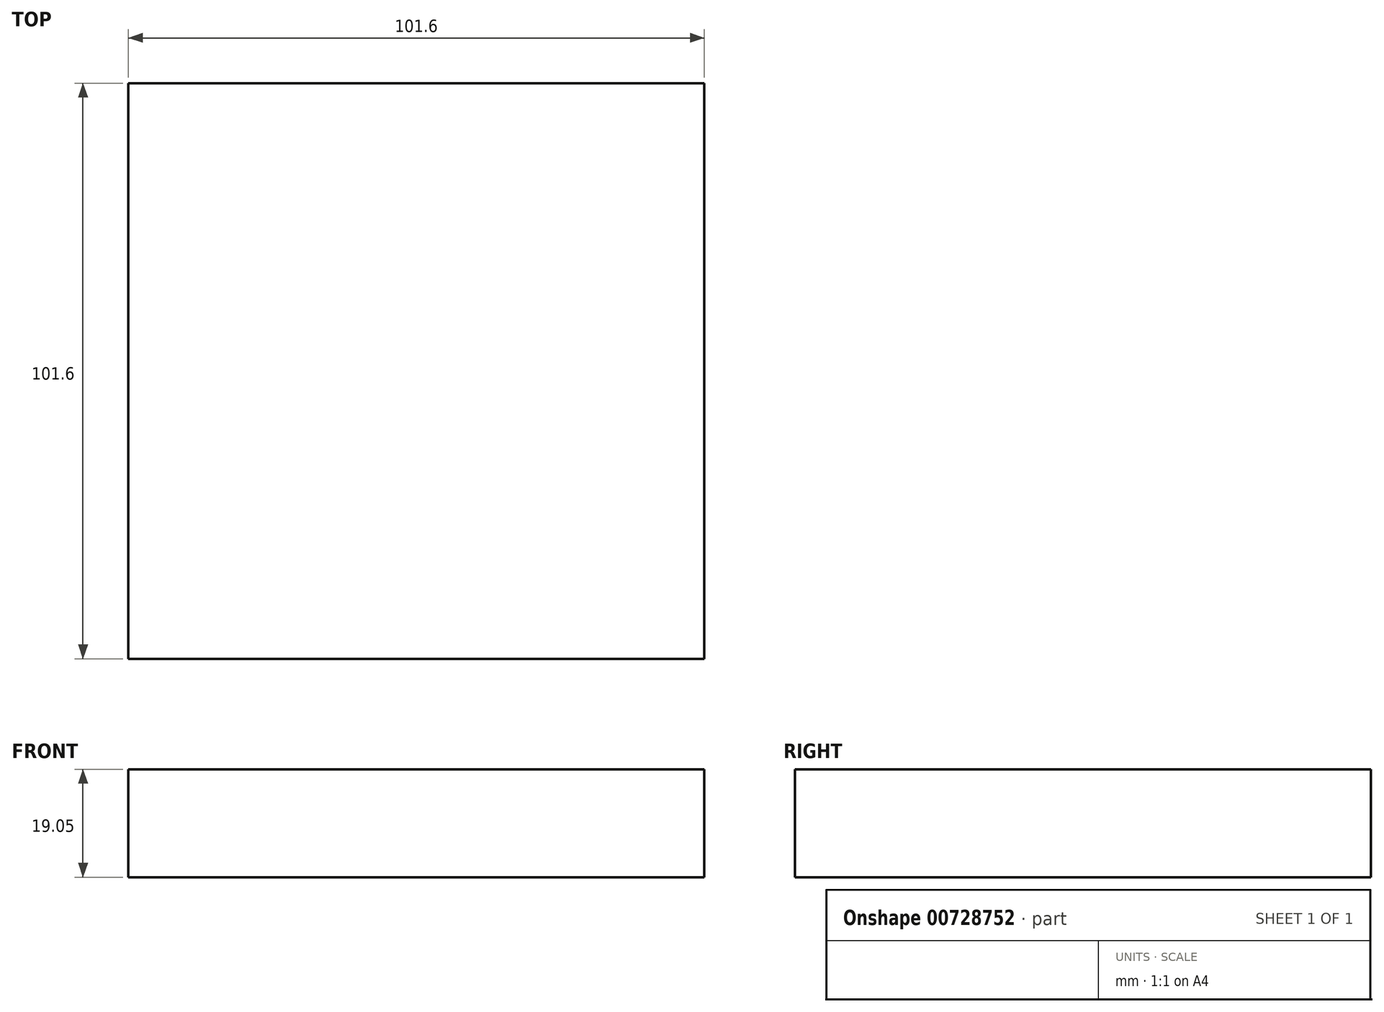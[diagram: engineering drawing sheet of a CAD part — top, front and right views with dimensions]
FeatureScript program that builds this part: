
annotation { "Feature Type Name" : "Feature", "Feature Type Description" : "" }
export const myFeature = defineFeature(function(context is Context, id is Id, definition is map)
    precondition{}
    {
        {
            var Q0;
            Q0=qCreatedBy(makeId("Top.planeOp"),FACE);
            var sketch = newSketch(context, id + "F0", { "sketchPlane" : qUnion([Q0])});
            skLineSegment(sketch, "E0.bottom", {"start": v(50.8, -50.8) * mm, "end": v(-50.8, -50.8) * mm});
            skLineSegment(sketch, "E0.top", {"start": v(50.8, 50.8) * mm, "end": v(-50.8, 50.8) * mm});
            skLineSegment(sketch, "E0.left", {"start": v(50.8, -50.8) * mm, "end": v(50.8, 50.8) * mm});
            skLineSegment(sketch, "E0.right", {"start": v(-50.8, -50.8) * mm, "end": v(-50.8, 50.8) * mm});
            skPoint(sketch, "E0.middle", {"position": v(0, 0) * mm});
            skSolve(sketch);
        }
        {
            var Q0;
            Q0 = qSketchRegion(id + "F0", true);
            extrude(context, id + "F1", {"entities" : qUnion([Q0]), "depth" : 19.05 * mm, "offsetDistance" : 25.4 * mm});
        }
    });
